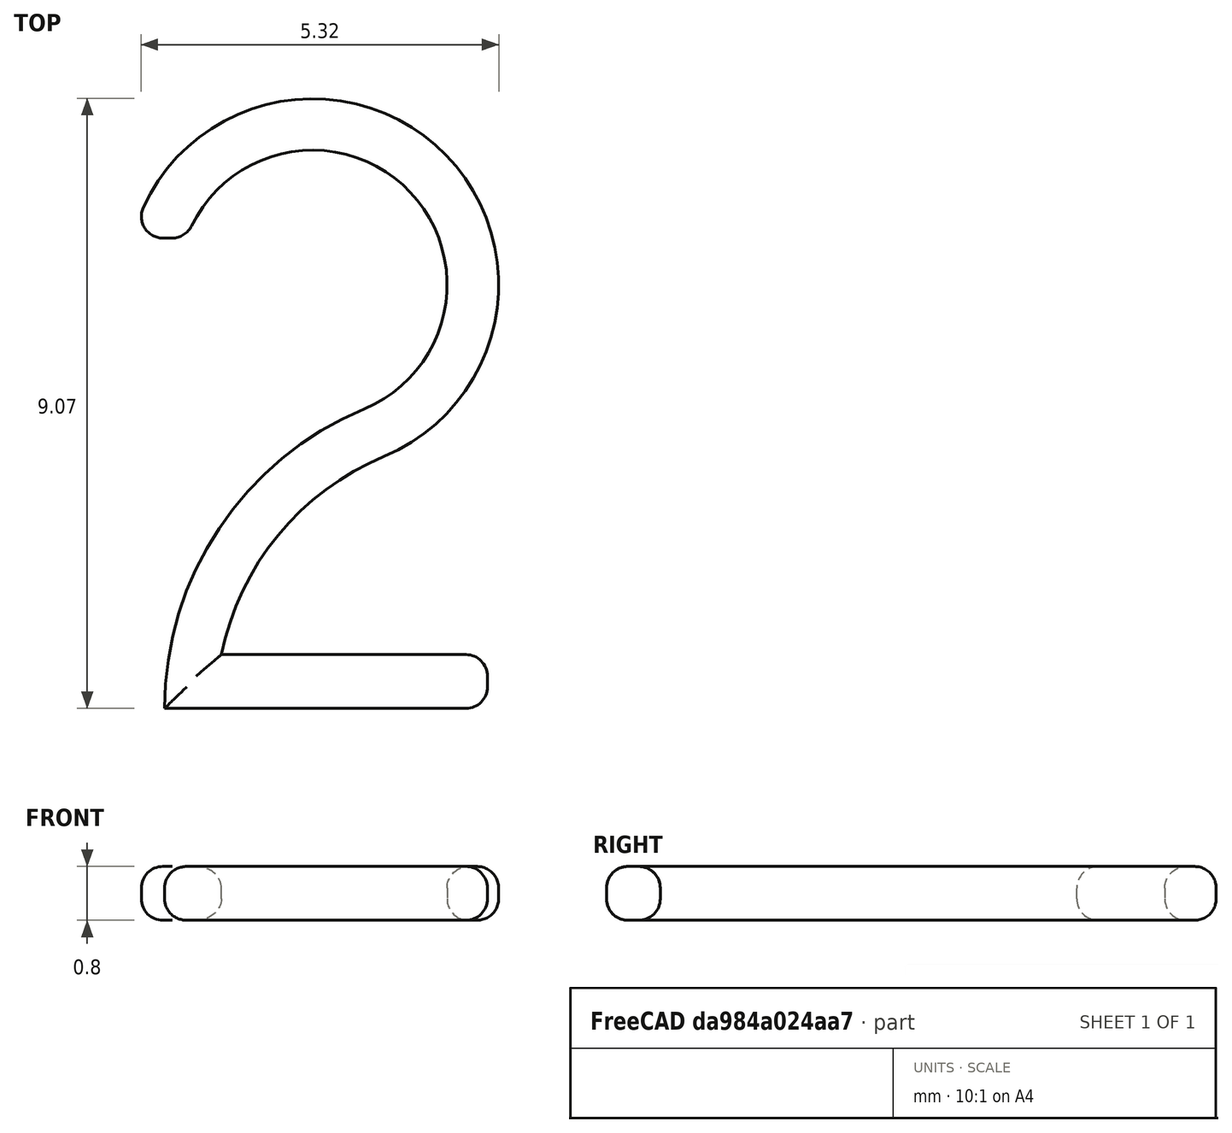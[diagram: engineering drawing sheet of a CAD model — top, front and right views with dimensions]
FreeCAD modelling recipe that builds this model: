
FCSTD DOCUMENT  (FreeCAD 0.16R6712 (Git))
Label: 2
License: All rights reserved
LicenseURL: http://en.wikipedia.org/wiki/All_rights_reserved
objects: Sketcher::SketchObject×1, PartDesign::Pad×1, PartDesign::Fillet×1, Mesh::Feature×1
note: 4 computed .brp shape members not serialized (recipe doc carries the construction recipe); baked Part::Feature solids carry a one-line shape summary decoded from their .brp

FEATURE [Sketcher::SketchObject] Sketch
  sketch-geometry (8):
    g0: ArcOfCircle CenterX=0 CenterY=6.3 CenterZ=0 NormalX=0 NormalY=0 NormalZ=1 Radius=2 StartAngle=5.10718 EndAngle=9.07158
    g1: LineSegment StartX=-2.2 StartY=0 StartZ=0 EndX=2.6 EndY=0 EndZ=0
    g2: ArcOfCircle CenterX=2.625 CenterY=0 CenterZ=0 NormalX=0 NormalY=0 NormalZ=1 Radius=4.825 StartAngle=1.96559 EndAngle=3.14159
    g3: ArcOfCircle CenterX=0 CenterY=6.3 CenterZ=0 NormalX=0 NormalY=0 NormalZ=1 Radius=2.7655 StartAngle=5.10718 EndAngle=9.17045
    g4: LineSegment StartX=2.6 StartY=0.8 StartZ=0 EndX=-1.35489 EndY=0.8 EndZ=0
    g5: LineSegment StartX=-2.67654 StartY=6.99579 StartZ=0 EndX=-1.87654 EndY=6.99181 EndZ=0
    g6: LineSegment StartX=2.6 StartY=0 StartZ=0 EndX=2.6 EndY=0.8 EndZ=0
    g7: ArcOfCircle CenterX=2.625 CenterY=0 CenterZ=0 NormalX=0 NormalY=0 NormalZ=1 Radius=4.0595 StartAngle=1.96559 EndAngle=2.94323
  constraints (25):
    c: PointOnObject(g0,g-2)
    c: PointOnObject(g1,g-1)
    c: PointOnObject(g1,g-1)
    c: Coincident(g2,g1)
    c: Radius(g0) = 2
    c: Coincident(g2,g0)
    c: DistanceY(g-1,g0) = 6.3
    c: Tangent(g0,g2)
    c: DistanceX(g-2,g1) = -2.2
    c: Distance(g-1,g1) = 2.6
    c: Coincident(g3,g0)
    c: Horizontal(g4)
    c: Coincident(g5,g3)
    c: Coincident(g5,g0)
    c: Coincident(g6,g1)
    c: Coincident(g6,g4)
    c: Vertical(g6)
    c: DistanceX(g3,g0) = 0.8
    c: DistanceY(g-1,g4) = 0.8
    c: Perpendicular(g2,g1)
    c: Coincident(g7,g2)
    c: Coincident(g7,g3)
    c: PointOnObject(g7,g4)
    c: Coincident(g4,g7)
    c: Tangent(g3,g7)
FEATURE [PartDesign::Pad] Pad
  Length = 0.8
  Length2 = 100
  Midplane = true
  Sketch = -> Sketch
  Type = 0
FEATURE [PartDesign::Fillet] Fillet
  Base = -> Pad [Edge3,Edge6,Edge9,Edge12,Edge15,Edge18,Edge21,Edge23,Edge20,Edge17,Edge22,Edge4,Edge7,Edge10,Edge13,Edge16,Edge19,Edge24,Edge8,Edge5]
  Radius = 0.32
FEATURE [Mesh::Feature] Mesh  label="Fillet (Meshed)"
